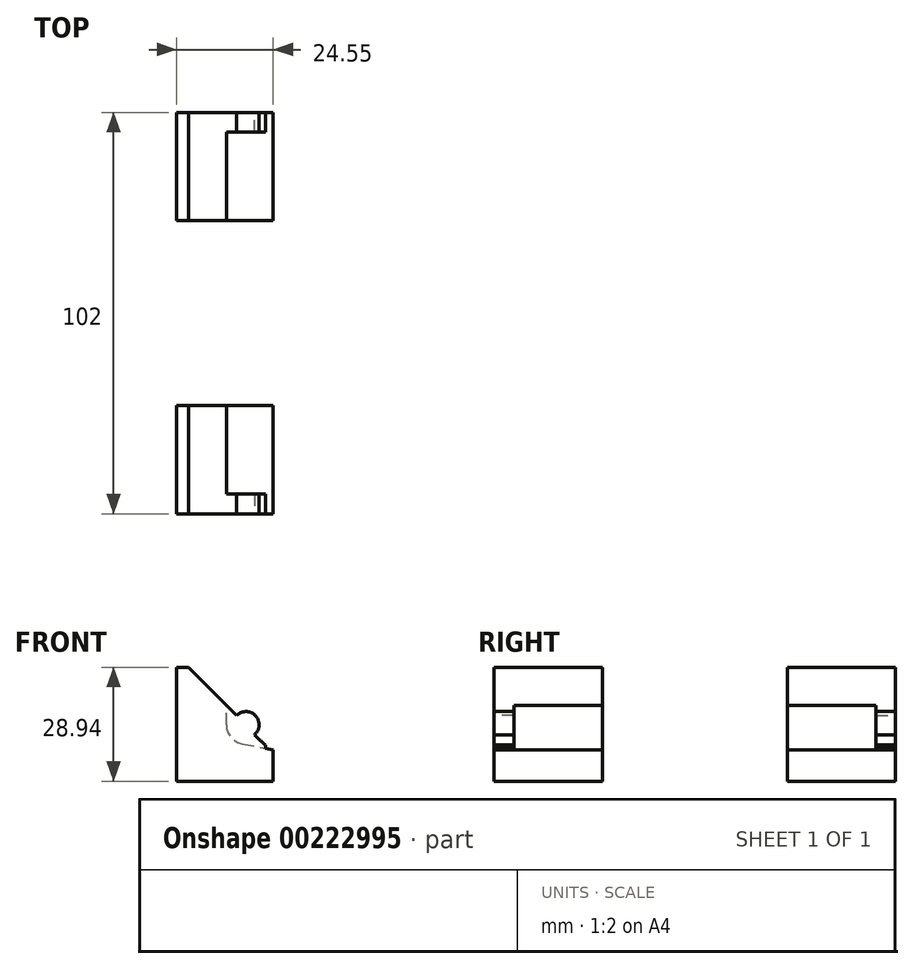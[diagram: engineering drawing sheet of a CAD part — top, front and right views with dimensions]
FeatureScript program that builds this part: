
annotation { "Feature Type Name" : "Feature", "Feature Type Description" : "" }
export const myFeature = defineFeature(function(context is Context, id is Id, definition is map)
    precondition{}
    {
        {
            var Q0;
            Q0=qCreatedBy(makeId("Front.planeOp"),FACE);
            var sketch = newSketch(context, id + "F0", { "sketchPlane" : qUnion([Q0])});
            skCircle(sketch, "E0", {"center": v(-26.85, 0) * mm, "radius": 3.35 * mm});
            skLineSegment(sketch, "E1", {"start": v(-31.8, -25.47) * mm, "end": v(-31.8, 0) * mm, "construction": true});
            skLineSegment(sketch, "E2", {"start": v(-30.2, -21.18) * mm, "end": v(-30.2, 0) * mm, "construction": true});
            skCircle(sketch, "E3", {"center": v(0, 21) * mm, "radius": 33 * mm, "construction": true});
            skLineSegment(sketch, "E4", {"start": v(-27.76, -4.87) * mm, "end": v(-19.9, -6.34) * mm});
            skLineSegment(sketch, "E5", {"start": v(-17.93, -6.7) * mm, "end": v(17.93, -6.7) * mm});
            skPoint(sketch, "E6", {"position": v(0, -6.7) * mm});
            skLineSegment(sketch, "E7", {"start": v(-31.8, -14.34) * mm, "end": v(-19.9, -14.34) * mm});
            skPoint(sketch, "E8", {"position": v(0, -13.71) * mm});
            skLineSegment(sketch, "E9", {"start": v(-31.8, 0) * mm, "end": v(-31.8, 4.95) * mm});
            skArc(sketch, "E10", {"start": v(-31.8, 0) * mm, "mid": v(-30.66, -3.16) * mm, "end": v(-27.76, -4.87) * mm});
            skArc(sketch, "E11", {"start": v(-21.9, 0) * mm, "mid": v(-23.35, 3.5) * mm, "end": v(-26.85, 4.95) * mm});
            skLineSegment(sketch, "E12", {"start": v(-21.9, 0) * mm, "end": v(-21.9, -5.96) * mm});
            skLineSegment(sketch, "E13", {"start": v(-31.8, -14.34) * mm, "end": v(-31.8, 4.95) * mm});
            skLineSegment(sketch, "E14", {"start": v(-26.85, 4.95) * mm, "end": v(-31.8, 4.95) * mm});
            skLineSegment(sketch, "E15", {"start": v(-19.9, -14.34) * mm, "end": v(-19.9, -6.34) * mm});
            skArc(sketch, "E16.trimOffspring", {"start": v(-24.66, -2.53) * mm, "mid": v(-23.32, -3.87) * mm, "end": v(-21.9, -5.12) * mm});
            skLineSegment(sketch, "E17", {"start": v(-31.8, -14.34) * mm, "end": v(-44.45, -14.34) * mm});
            skLineSegment(sketch, "E18", {"start": v(-44.45, -14.34) * mm, "end": v(-44.45, 14.6) * mm});
            skLineSegment(sketch, "E19", {"start": v(-44.45, 14.6) * mm, "end": v(-41.45, 14.6) * mm});
            skLineSegment(sketch, "E20", {"start": v(-41.45, 14.6) * mm, "end": v(-29.22, 2.37) * mm});
            skSolve(sketch);
        }
        {
            var Q0;
            Q0=makeQuery(id+"F0.imprint","IMPRINT",FACE,{"disambiguationData":[TD([[makeQuery(id+"F0.imprint","IMPRINT",EDGE,{"derivedFrom":sQuery(id+"F0.wireOp",EDGE,"E4")}),-1.0]])]});
            var Q1;
            {var subQ0=sQuery(id+"F0.wireOp",EDGE,"lqltnO4p-yjQs-zU1a-pGAH-Qr9mpKHK8XKR");Q1=makeQuery(id+"F0.imprint","IMPRINT",FACE,{"disambiguationData":[TD([[makeQuery(id+"F0.imprint","IMPRINT",EDGE,{"derivedFrom":subQ0}),1.0]])]});}
            var Q2;
            Q2=makeQuery(id+"F0.imprint","IMPRINT",FACE,{"disambiguationData":[TD([[makeQuery(id+"F0.imprint","IMPRINT",EDGE,{"derivedFrom":sQuery(id+"F0.wireOp",EDGE,"UlOUm8Tg-GByg-MkmW-qwdk-OexTPjV0Y8lK")}),-1.0]])]});
            var Q3;
            {var subQ0=sQuery(id+"F0.wireOp",EDGE,"E17");Q3=makeQuery(id+"F0.imprint","IMPRINT",FACE,{"disambiguationData":[TD([[makeQuery(id+"F0.imprint","IMPRINT",EDGE,{"derivedFrom":subQ0}),-1.0]])]});}
            extrude(context, id + "F1", {"entities" : qUnion([Q0, Q1, Q2, Q3]), "depth" : 27.5 * mm});
        }
        {
            var Q0;
            {var subQ4=sQuery(id+"F0.wireOp",EDGE,"E10");Q0=makeQuery(id+"F0.imprint","IMPRINT",FACE,{"disambiguationData":[TD([[makeQuery(id+"F0.imprint","IMPRINT",EDGE,{"derivedFrom":subQ4}),1.0]])]});}
            var Q1;
            {var subQ0=sQuery(id+"F0.wireOp",EDGE,"E0");var subQ1=makeQuery(id+"F0.imprint","INTERSECT",VERTEX,{"derivedFrom":[subQ0,sQuery(id+"F0.wireOp",EDGE,"MtPSfYva-7y9Z-Twtf-idye-PItontqrztNB")]});Q1=makeQuery(id+"F0.imprint","IMPRINT",FACE,{"disambiguationData":[TD([[makeQuery(id+"F0.imprint","IMPRINT",EDGE,{"disambiguationData":[TD([[subQ1,-1.0]])],"derivedFrom":subQ0}),1.0]])]});}
            var Q2;
            Q2=makeQuery(id+"F1.opExtrude","CAP_FACE",FACE,{"disambiguationData":[OSD([sQuery(id+"F0.wireOp",EDGE,"E4"),sQuery(id+"F0.wireOp",EDGE,"hitLcRcT-vsjn-UHvc-ALBO-6uXqSwUWMRml"),sQuery(id+"F0.wireOp",EDGE,"E7"),sQuery(id+"F0.wireOp",EDGE,"E9"),sQuery(id+"F0.wireOp",EDGE,"5h00GBxq-CeBK-yBVB-LUKm-K3VklLHiz7XQ"),sQuery(id+"F0.wireOp",EDGE,"lqltnO4p-yjQs-zU1a-pGAH-Qr9mpKHK8XKR"),sQuery(id+"F0.wireOp",EDGE,"E10")])],"isStart":true});
            extrude(context, id + "F2", {"entities" : qUnion([Q0, Q1]), "operationType" : NewBodyOperationType.ADD, "depth" : 5 * mm});
        }
        {
            var Q0;
            Q0=makeQuery(id+"F1.opExtrude","SWEPT_BODY",BODY,{"disambiguationData":[OSD([sQuery(id+"F0.wireOp",EDGE,"E4"),sQuery(id+"F0.wireOp",EDGE,"hitLcRcT-vsjn-UHvc-ALBO-6uXqSwUWMRml"),sQuery(id+"F0.wireOp",EDGE,"E7"),sQuery(id+"F0.wireOp",EDGE,"E9"),sQuery(id+"F0.wireOp",EDGE,"5h00GBxq-CeBK-yBVB-LUKm-K3VklLHiz7XQ"),sQuery(id+"F0.wireOp",EDGE,"lqltnO4p-yjQs-zU1a-pGAH-Qr9mpKHK8XKR"),sQuery(id+"F0.wireOp",EDGE,"E10")])]});
            var Q1;
            Q1=makeQuery(id+"F1.opExtrude","SWEPT_EDGE",EDGE,{"disambiguationData":[OSD([sQuery(id+"F0.wireOp",EDGE,"hitLcRcT-vsjn-UHvc-ALBO-6uXqSwUWMRml"),sQuery(id+"F0.wireOp",EDGE,"E7")])]});
            transform(context, id + "F3", {"entities" : qUnion([Q0]), "transformType" : TransformType.TRANSLATION_DISTANCE, "transformDirection" : qUnion([Q1]), "distance" : (44 + 2 + 5) * mm, "makeCopy" : false});
        }
        {
            var Q0;
            Q0=makeQuery(id+"F1.opExtrude","SWEPT_BODY",BODY,{"disambiguationData":[OSD([sQuery(id+"F0.wireOp",EDGE,"E4"),sQuery(id+"F0.wireOp",EDGE,"hitLcRcT-vsjn-UHvc-ALBO-6uXqSwUWMRml"),sQuery(id+"F0.wireOp",EDGE,"E7"),sQuery(id+"F0.wireOp",EDGE,"E9"),sQuery(id+"F0.wireOp",EDGE,"5h00GBxq-CeBK-yBVB-LUKm-K3VklLHiz7XQ"),sQuery(id+"F0.wireOp",EDGE,"lqltnO4p-yjQs-zU1a-pGAH-Qr9mpKHK8XKR"),sQuery(id+"F0.wireOp",EDGE,"E10")])]});
            var Q1;
            Q1=qCreatedBy(makeId("Front.planeOp"),FACE);
            mirror(context, id + "F4", {"entities" : qUnion([Q0]), "mirrorPlane" : qUnion([Q1])});
        }
    });
